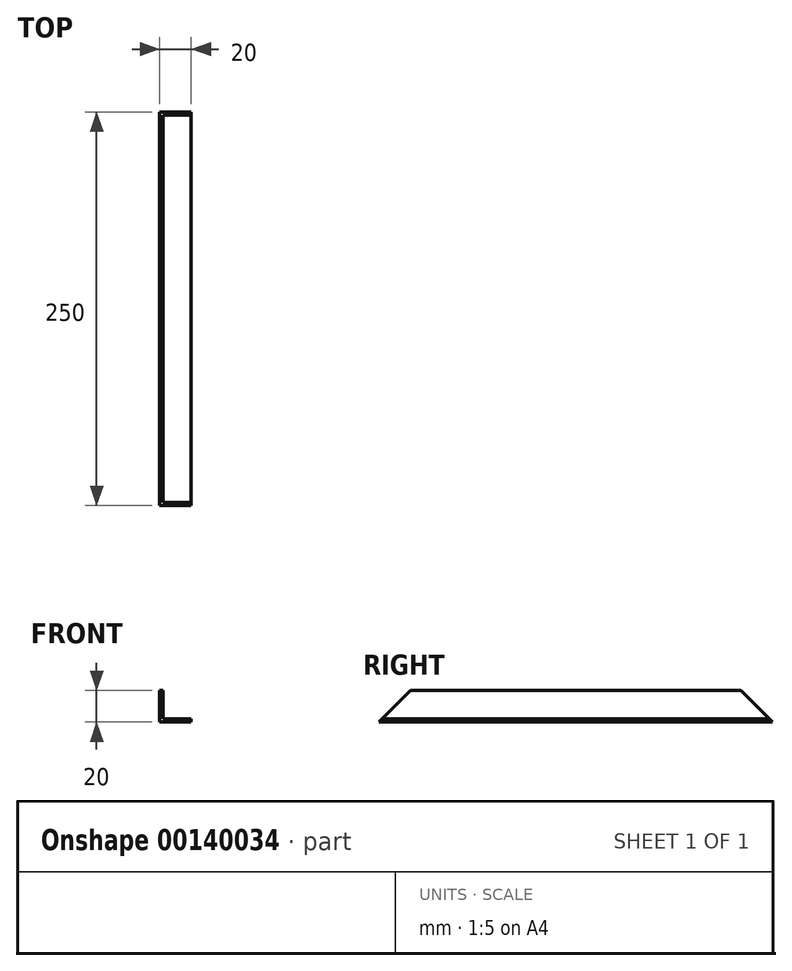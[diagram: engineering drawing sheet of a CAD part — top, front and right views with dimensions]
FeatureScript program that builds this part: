
annotation { "Feature Type Name" : "Feature", "Feature Type Description" : "" }
export const myFeature = defineFeature(function(context is Context, id is Id, definition is map)
    precondition{}
    {
        {
            var Q0;
            Q0=qCreatedBy(makeId("Front.planeOp"),FACE);
            var sketch = newSketch(context, id + "F0", { "sketchPlane" : qUnion([Q0])});
            skLineSegment(sketch, "E0", {"start": v(0, 0) * mm, "end": v(20, 0) * mm});
            skLineSegment(sketch, "E1", {"start": v(20, 0) * mm, "end": v(20, 2) * mm});
            skLineSegment(sketch, "E2", {"start": v(20, 2) * mm, "end": v(2, 2) * mm});
            skLineSegment(sketch, "E3", {"start": v(2, 2) * mm, "end": v(2, 20) * mm});
            skLineSegment(sketch, "E4", {"start": v(2, 20) * mm, "end": v(0, 20) * mm});
            skLineSegment(sketch, "E5", {"start": v(0, 20) * mm, "end": v(0, 0) * mm});
            skSolve(sketch);
        }
        {
            var Q0;
            Q0=qSketchRegion(id+"F0",true);
            extrude(context, id + "F1", {"entities" : qUnion([Q0]), "endBound" : BoundingType.SYMMETRIC, "depth" : 250 * mm});
        }
        {
            var Q0;
            Q0=makeQuery(id+"F1.opExtrude","SWEPT_FACE",FACE,{"disambiguationData":[OSD([sQuery(id+"F0.wireOp",EDGE,"E5")])]});
            var sketch = newSketch(context, id + "F2", { "sketchPlane" : qUnion([Q0])});
            skLineSegment(sketch, "E6", {"start": v(-125, 0) * mm, "end": v(-105, 20) * mm});
            skLineSegment(sketch, "E7", {"start": v(-105, 20) * mm, "end": v(-125, 20) * mm});
            skLineSegment(sketch, "E8", {"start": v(-125, 20) * mm, "end": v(-125, 0) * mm});
            skLineSegment(sketch, "E9.MirrorCS", {"start": v(125, 20) * mm, "end": v(125, 0) * mm});
            skLineSegment(sketch, "E10.MirrorCS", {"start": v(105, 20) * mm, "end": v(125, 20) * mm});
            skLineSegment(sketch, "E11.MirrorCS", {"start": v(125, 0) * mm, "end": v(105, 20) * mm});
            skSolve(sketch);
        }
        {
            var Q0;
            Q0=qSketchRegion(id+"F2",true);
            extrude(context, id + "F3", {"entities" : qUnion([Q0]), "operationType" : NewBodyOperationType.REMOVE, "endBound" : BoundingType.THROUGH_ALL, "oppositeDirection" : true, "depth" : 25.4 * mm});
        }
        {
            var Q0;
            Q0=makeQuery(id+"F1.opExtrude","SWEPT_BODY",BODY,{"disambiguationData":[OSD([sQuery(id+"F0.wireOp",EDGE,"E0"),sQuery(id+"F0.wireOp",EDGE,"E1"),sQuery(id+"F0.wireOp",EDGE,"E2"),sQuery(id+"F0.wireOp",EDGE,"E3"),sQuery(id+"F0.wireOp",EDGE,"E4"),sQuery(id+"F0.wireOp",EDGE,"E5")])]});
            transform(context, id + "F4", {"entities" : qUnion([Q0]), "transformType" : TransformType.TRANSLATION_3D, "dx" : 0 * mm, "dy" : 0 * mm, "dz" : 0 * mm, "makeCopy" : true});
        }
        {
            var Q0;
            Q0=makeQuery(id+"F1.opExtrude","SWEPT_BODY",BODY,{"disambiguationData":[OSD([sQuery(id+"F0.wireOp",EDGE,"E0"),sQuery(id+"F0.wireOp",EDGE,"E1"),sQuery(id+"F0.wireOp",EDGE,"E2"),sQuery(id+"F0.wireOp",EDGE,"E3"),sQuery(id+"F0.wireOp",EDGE,"E4"),sQuery(id+"F0.wireOp",EDGE,"E5")])]});
            deleteBodies(context, id + "F5", {"entities" : qUnion([Q0])});
        }
    });
